# Revit family: RS Søjler Spæncom
name_source: partatom
category: Structural Columns
revit_build: Autodesk Revit 2014 (Build: 20130308_1515(x64)
units: mm (PartAtom-declared; Revit-internal decimal feet)

## types (84) — shared parameters
Manufacturer = Spæncom
Søjle længde = 4000 mm  [stored 13.1234 ft]

## per-type parameters (varying)
| type | Depth | Width |
| RS18/24 | 180 mm  [stored 0.590551 ft] | 240 mm  [stored 0.787402 ft] |
| RS18/30 | 180 mm  [stored 0.590551 ft] | 300 mm |
| RS18/36 | 180 mm  [stored 0.590551 ft] | 360 mm  [stored 1.1811 ft] |
| RS18/42 | 180 mm  [stored 0.590551 ft] | 420 mm  [stored 1.37795 ft] |
| RS18/48 | 180 mm  [stored 0.590551 ft] | 480 mm  [stored 1.5748 ft] |
| RS18/50 | 180 mm  [stored 0.590551 ft] | 500 mm  [stored 1.64042 ft] |
| RS18/60 | 180 mm  [stored 0.590551 ft] | 600 mm |
| RS18/72 | 180 mm  [stored 0.590551 ft] | 720 mm  [stored 2.3622 ft] |
| RS18/84 | 180 mm  [stored 0.590551 ft] | 840 mm  [stored 2.75591 ft] |
| RS24/24 | 240 mm  [stored 0.787402 ft] | 240 mm  [stored 0.787402 ft] |
| RS24/30 | 240 mm  [stored 0.787402 ft] | 300 mm |
| RS24/36 | 240 mm  [stored 0.787402 ft] | 360 mm  [stored 1.1811 ft] |
| RS24/42 | 240 mm  [stored 0.787402 ft] | 420 mm  [stored 1.37795 ft] |
| RS24/48 | 240 mm  [stored 0.787402 ft] | 480 mm  [stored 1.5748 ft] |
| RS24/50 | 240 mm  [stored 0.787402 ft] | 500 mm  [stored 1.64042 ft] |
| RS24/60 | 240 mm  [stored 0.787402 ft] | 600 mm |
| RS24/72 | 240 mm  [stored 0.787402 ft] | 720 mm  [stored 2.3622 ft] |
| RS24/84 | 240 mm  [stored 0.787402 ft] | 840 mm  [stored 2.75591 ft] |
| RS30/30 | 300 mm | 300 mm |
| RS30/36 | 300 mm | 360 mm  [stored 1.1811 ft] |
| RS30/42 | 300 mm | 420 mm  [stored 1.37795 ft] |
| RS30/48 | 300 mm | 480 mm  [stored 1.5748 ft] |
| RS30/50 | 300 mm | 500 mm  [stored 1.64042 ft] |
| RS30/60 | 300 mm | 600 mm |
| RS30/72 | 300 mm | 720 mm  [stored 2.3622 ft] |
| RS30/84 | 300 mm | 840 mm  [stored 2.75591 ft] |
| RS36/36 | 360 mm  [stored 1.1811 ft] | 360 mm  [stored 1.1811 ft] |
| RS36/42 | 360 mm  [stored 1.1811 ft] | 420 mm  [stored 1.37795 ft] |
| RS36/48 | 360 mm  [stored 1.1811 ft] | 480 mm  [stored 1.5748 ft] |
| RS36/50 | 360 mm  [stored 1.1811 ft] | 500 mm  [stored 1.64042 ft] |
| RS36/60 | 360 mm  [stored 1.1811 ft] | 600 mm |
| RS36/72 | 360 mm  [stored 1.1811 ft] | 720 mm  [stored 2.3622 ft] |
| RS36/84 | 360 mm  [stored 1.1811 ft] | 840 mm  [stored 2.75591 ft] |
| RS42/42 | 420 mm  [stored 1.37795 ft] | 420 mm  [stored 1.37795 ft] |
| RS42/48 | 420 mm  [stored 1.37795 ft] | 480 mm  [stored 1.5748 ft] |
| RS42/50 | 420 mm  [stored 1.37795 ft] | 500 mm  [stored 1.64042 ft] |
| RS42/60 | 420 mm  [stored 1.37795 ft] | 600 mm |
| RS42/72 | 420 mm  [stored 1.37795 ft] | 720 mm  [stored 2.3622 ft] |
| RS42/84 | 420 mm  [stored 1.37795 ft] | 840 mm  [stored 2.75591 ft] |
| RS48/48 | 480 mm  [stored 1.5748 ft] | 480 mm  [stored 1.5748 ft] |
| RS48/50 | 480 mm  [stored 1.5748 ft] | 500 mm  [stored 1.64042 ft] |
| RS48/60 | 480 mm  [stored 1.5748 ft] | 600 mm |
| RS48/72 | 480 mm  [stored 1.5748 ft] | 720 mm  [stored 2.3622 ft] |
| RS48/84 | 480 mm  [stored 1.5748 ft] | 840 mm  [stored 2.75591 ft] |
| RS54/50 | 540 mm  [stored 1.77165 ft] | 500 mm  [stored 1.64042 ft] |
| RS54/60 | 540 mm  [stored 1.77165 ft] | 600 mm |
| RS54/72 | 540 mm  [stored 1.77165 ft] | 720 mm  [stored 2.3622 ft] |
| RS54/84 | 540 mm  [stored 1.77165 ft] | 840 mm  [stored 2.75591 ft] |
| RS60/60 | 600 mm | 600 mm |
| RS60/72 | 600 mm | 720 mm  [stored 2.3622 ft] |
| RS60/84 | 600 mm | 840 mm  [stored 2.75591 ft] |
| RS72/72 | 720 mm  [stored 2.3622 ft] | 720 mm  [stored 2.3622 ft] |
| RS72/84 | 720 mm  [stored 2.3622 ft] | 840 mm  [stored 2.75591 ft] |
| RS84/84 | 840 mm  [stored 2.75591 ft] | 840 mm  [stored 2.75591 ft] |
| RS108/18 | 1080 mm  [stored 3.54331 ft] | 180 mm  [stored 0.590551 ft] |
| RS108/24 | 1080 mm  [stored 3.54331 ft] | 240 mm  [stored 0.787402 ft] |
| RS108/30 | 1080 mm  [stored 3.54331 ft] | 300 mm |
| RS108/36 | 1080 mm  [stored 3.54331 ft] | 360 mm  [stored 1.1811 ft] |
| RS108/42 | 1080 mm  [stored 3.54331 ft] | 420 mm  [stored 1.37795 ft] |
| RS108/48 | 1080 mm  [stored 3.54331 ft] | 480 mm  [stored 1.5748 ft] |
| RS108/50 | 1080 mm  [stored 3.54331 ft] | 500 mm  [stored 1.64042 ft] |
| RS108/60 | 1080 mm  [stored 3.54331 ft] | 600 mm |
| RS108/72 | 1080 mm  [stored 3.54331 ft] | 720 mm  [stored 2.3622 ft] |
| RS108/84 | 1080 mm  [stored 3.54331 ft] | 840 mm  [stored 2.75591 ft] |
| RS120/18 | 1200 mm | 180 mm  [stored 0.590551 ft] |
| RS120/24 | 1200 mm | 240 mm  [stored 0.787402 ft] |
| RS120/30 | 1200 mm | 300 mm |
| RS120/36 | 1200 mm | 360 mm  [stored 1.1811 ft] |
| RS120/42 | 1200 mm | 420 mm  [stored 1.37795 ft] |
| RS120/48 | 1200 mm | 480 mm  [stored 1.5748 ft] |
| RS120/50 | 1200 mm | 500 mm  [stored 1.64042 ft] |
| RS120/60 | 1200 mm | 600 mm |
| RS120/72 | 1200 mm | 720 mm  [stored 2.3622 ft] |
| RS120/84 | 1200 mm | 840 mm  [stored 2.75591 ft] |
| RS140/18 | 1400 mm  [stored 4.59318 ft] | 180 mm  [stored 0.590551 ft] |
| RS140/24 | 1400 mm  [stored 4.59318 ft] | 240 mm  [stored 0.787402 ft] |
| RS140/30 | 1400 mm  [stored 4.59318 ft] | 300 mm |
| RS140/36 | 1400 mm  [stored 4.59318 ft] | 360 mm  [stored 1.1811 ft] |
| RS140/42 | 1400 mm  [stored 4.59318 ft] | 420 mm  [stored 1.37795 ft] |
| RS140/48 | 1400 mm  [stored 4.59318 ft] | 480 mm  [stored 1.5748 ft] |
| RS140/50 | 1400 mm  [stored 4.59318 ft] | 500 mm  [stored 1.64042 ft] |
| RS140/60 | 1400 mm  [stored 4.59318 ft] | 600 mm |
| RS140/72 | 1400 mm  [stored 4.59318 ft] | 720 mm  [stored 2.3622 ft] |
| RS140/84 | 1400 mm  [stored 4.59318 ft] | 840 mm  [stored 2.75591 ft] |

note: [stored X ft] marks values corroborated as IEEE doubles in the binary element streams (Revit-internal decimal feet)

## geometry (parser evidence)
native form markers: Sweep x6
no freeform markers — native parametric forms only
